FCSTD DOCUMENT  (FreeCAD 0.21R33675 (Git))
Label: Radio Nav Enclosure
License: All rights reserved
LicenseURL: https://en.wikipedia.org/wiki/All_rights_reserved
objects: Sketcher::SketchObject×1, PartDesign::Body×1
note: 2 computed .brp shape members not serialized (recipe doc carries the construction recipe); baked Part::Feature solids carry a one-line shape summary decoded from their .brp

FEATURE [Sketcher::SketchObject] Sketch  label="Radio Nav Enclosure Baseplate Sketch"
  FullyConstrained = true
  MapMode = 5
  Support = -> [XY_Plane]
  sketch-geometry (4):
    g0: LineSegment StartX=-89 StartY=72.5 StartZ=0 EndX=89 EndY=72.5 EndZ=0
    g1: LineSegment StartX=89 StartY=72.5 StartZ=0 EndX=89 EndY=-72.5 EndZ=0
    g2: LineSegment StartX=89 StartY=-72.5 StartZ=0 EndX=-89 EndY=-72.5 EndZ=0
    g3: LineSegment StartX=-89 StartY=-72.5 StartZ=0 EndX=-89 EndY=72.5 EndZ=0
  constraints (10):
    c: Coincident(g0,g1)
    c: Coincident(g1,g2)
    c: Coincident(g2,g3)
    c: Coincident(g3,g0)
    c: Horizontal(g2)
    c: Vertical(g1)
    c: Symmetric(g0,g0,g-2)
    c: Symmetric(g0,g2,g-1)
    c: DistanceX(g0,g0) = 178
    c: DistanceY(g3,g3) = 145
FEATURE [PartDesign::Body] Body  label="Radio Nav Enclosure Stator"
  Group = -> [Sketch]
  Origin = -> Origin
